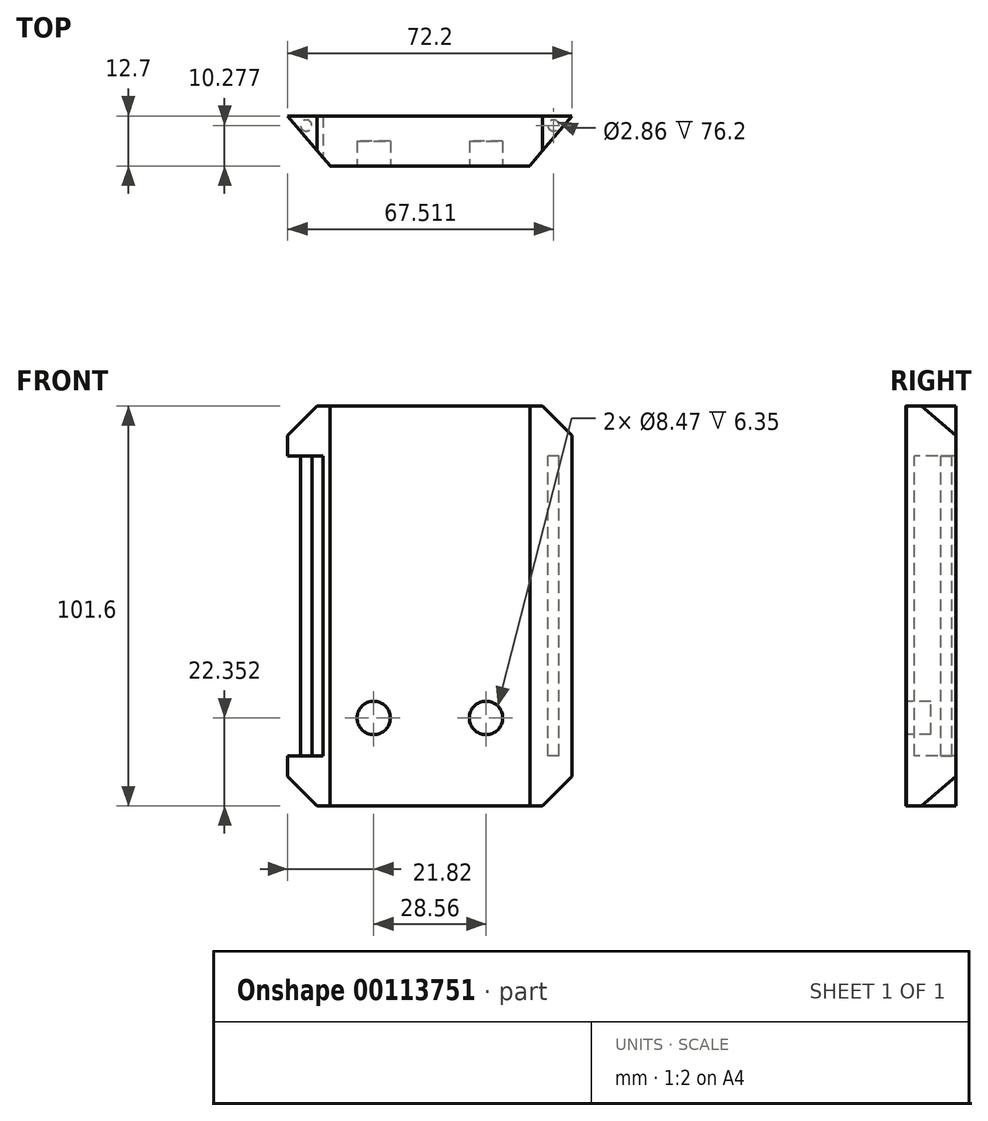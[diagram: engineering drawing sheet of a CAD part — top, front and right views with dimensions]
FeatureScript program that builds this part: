
annotation { "Feature Type Name" : "Feature", "Feature Type Description" : "" }
export const myFeature = defineFeature(function(context is Context, id is Id, definition is map)
    precondition{}
    {
        {
            var Q0;
            Q0=qCreatedBy(makeId("Front.planeOp"),FACE);
            var sketch = newSketch(context, id + "F0", { "sketchPlane" : qUnion([Q0])});
            skLineSegment(sketch, "E0.bottom", {"start": v(25.4, 50.8) * mm, "end": v(-25.4, 50.8) * mm});
            skLineSegment(sketch, "E0.top", {"start": v(25.4, -50.8) * mm, "end": v(-25.4, -50.8) * mm});
            skLineSegment(sketch, "E0.left", {"start": v(25.4, 50.8) * mm, "end": v(25.4, -50.8) * mm});
            skLineSegment(sketch, "E0.right", {"start": v(-25.4, 50.8) * mm, "end": v(-25.4, -50.8) * mm});
            skPoint(sketch, "E0.middle", {"position": v(0, 0) * mm});
            skSolve(sketch);
        }
        {
            var Q0;
            Q0=qSketchRegion(id+"F0",true);
            extrude(context, id + "F1", {"entities" : qUnion([Q0]), "depth" : 12.7 * mm});
        }
        {
            var Q0;
            Q0=qCreatedBy(makeId("Top.planeOp"),FACE);
            var sketch = newSketch(context, id + "F2", { "sketchPlane" : qUnion([Q0])});
            skLineSegment(sketch, "E1", {"start": v(25.4, 0) * mm, "end": v(36.1, 0) * mm});
            skLineSegment(sketch, "E2", {"start": v(36.1, 0) * mm, "end": v(25.4, -12.67) * mm});
            skLineSegment(sketch, "E3", {"start": v(25.4, -12.67) * mm, "end": v(25.4, 0) * mm});
            skLineSegment(sketch, "E4.MirrorCS", {"start": v(-36.1, 0) * mm, "end": v(-25.4, -12.67) * mm});
            skLineSegment(sketch, "E5.MirrorCS", {"start": v(-25.4, -12.67) * mm, "end": v(-25.4, 0) * mm});
            skLineSegment(sketch, "E6.MirrorCS", {"start": v(-25.4, 0) * mm, "end": v(-36.1, 0) * mm});
            skSolve(sketch);
        }
        {
            var Q0;
            Q0=qSketchRegion(id+"F2",true);
            extrude(context, id + "F3", {"entities" : qUnion([Q0]), "operationType" : NewBodyOperationType.ADD, "depth" : 101.6 * mm, "symmetric" : true});
        }
        {
            var Q0;
            Q0=qCreatedBy(makeId("Top.planeOp"),FACE);
            var sketch = newSketch(context, id + "F4", { "sketchPlane" : qUnion([Q0])});
            skCircle(sketch, "E7", {"center": v(-31.41, -2.42) * mm, "radius": 1.43 * mm});
            skCircle(sketch, "E8.MirrorC", {"center": v(31.41, -2.42) * mm, "radius": 1.43 * mm});
            skLineSegment(sketch, "E9.bottom", {"start": v(27.18, 1.43) * mm, "end": v(39.9, 1.43) * mm});
            skLineSegment(sketch, "E9.top", {"start": v(27.18, -11.19) * mm, "end": v(39.9, -11.19) * mm});
            skLineSegment(sketch, "E9.left", {"start": v(27.18, 1.43) * mm, "end": v(27.18, -11.19) * mm});
            skLineSegment(sketch, "E9.right", {"start": v(39.9, 1.43) * mm, "end": v(39.9, -11.19) * mm});
            skLineSegment(sketch, "E10.MirrorCS", {"start": v(-27.18, -11.19) * mm, "end": v(-39.9, -11.19) * mm});
            skLineSegment(sketch, "E11.MirrorCS", {"start": v(-39.9, 1.43) * mm, "end": v(-39.9, -11.19) * mm});
            skLineSegment(sketch, "E12.MirrorCS", {"start": v(-27.18, 1.43) * mm, "end": v(-39.9, 1.43) * mm});
            skLineSegment(sketch, "E13.MirrorCS", {"start": v(-27.18, 1.43) * mm, "end": v(-27.18, -11.19) * mm});
            skSolve(sketch);
        }
        {
            var Q0;
            Q0=makeQuery(id+"F4.imprint","IMPRINT",FACE,{"disambiguationData":[TD([[makeQuery(id+"F4.imprint","IMPRINT",EDGE,{"derivedFrom":sQuery(id+"F4.wireOp",EDGE,"E8.MirrorC")}),1.0]])]});
            var Q1;
            Q1=makeQuery(id+"F4.imprint","IMPRINT",FACE,{"disambiguationData":[TD([[makeQuery(id+"F4.imprint","IMPRINT",EDGE,{"derivedFrom":sQuery(id+"F4.wireOp",EDGE,"E7")}),-1.0]])]});
            extrude(context, id + "F5", {"entities" : qUnion([Q0, Q1]), "operationType" : NewBodyOperationType.REMOVE, "oppositeDirection" : true, "depth" : 76.2 * mm, "symmetric" : true});
        }
        {
            var Q0;
            Q0=qCreatedBy(makeId("Front.planeOp"),FACE);
            var sketch = newSketch(context, id + "F6", { "sketchPlane" : qUnion([Q0])});
            skLineSegment(sketch, "E14", {"start": v(-40.53, 38.9) * mm, "end": v(-23.28, 56.16) * mm});
            skLineSegment(sketch, "E15", {"start": v(-23.28, 56.16) * mm, "end": v(-40.53, 56.16) * mm});
            skLineSegment(sketch, "E16", {"start": v(-40.53, 56.16) * mm, "end": v(-40.53, 38.9) * mm});
            skLineSegment(sketch, "E17.MirrorCS", {"start": v(40.53, 56.16) * mm, "end": v(40.53, 38.9) * mm});
            skLineSegment(sketch, "E18.MirrorCS", {"start": v(23.28, 56.16) * mm, "end": v(40.53, 56.16) * mm});
            skLineSegment(sketch, "E19.MirrorCS", {"start": v(40.53, 38.9) * mm, "end": v(23.28, 56.16) * mm});
            skLineSegment(sketch, "E20.MirrorCS", {"start": v(-40.53, -56.16) * mm, "end": v(-40.53, -38.9) * mm});
            skLineSegment(sketch, "E21.MirrorCS", {"start": v(-23.28, -56.16) * mm, "end": v(-40.53, -56.16) * mm});
            skLineSegment(sketch, "E22.MirrorCS", {"start": v(-40.53, -38.9) * mm, "end": v(-23.28, -56.16) * mm});
            skLineSegment(sketch, "E23.MirrorCS", {"start": v(40.53, -38.9) * mm, "end": v(23.28, -56.16) * mm});
            skLineSegment(sketch, "E24.MirrorCS", {"start": v(23.28, -56.16) * mm, "end": v(40.53, -56.16) * mm});
            skLineSegment(sketch, "E25.MirrorCS", {"start": v(40.53, -56.16) * mm, "end": v(40.53, -38.9) * mm});
            skSolve(sketch);
        }
        {
            var Q0;
            Q0=makeQuery(id+"F6.imprint","IMPRINT",FACE,{"disambiguationData":[TD([[makeQuery(id+"F6.imprint","IMPRINT",EDGE,{"derivedFrom":sQuery(id+"F6.wireOp",EDGE,"E17.MirrorCS")}),-1.0]])]});
            var Q1;
            Q1=makeQuery(id+"F6.imprint","IMPRINT",FACE,{"disambiguationData":[TD([[makeQuery(id+"F6.imprint","IMPRINT",EDGE,{"derivedFrom":sQuery(id+"F6.wireOp",EDGE,"E20.MirrorCS")}),-1.0]])]});
            var Q2;
            Q2=makeQuery(id+"F6.imprint","IMPRINT",FACE,{"disambiguationData":[TD([[makeQuery(id+"F6.imprint","IMPRINT",EDGE,{"derivedFrom":sQuery(id+"F6.wireOp",EDGE,"E23.MirrorCS")}),1.0]])]});
            var Q3;
            Q3=makeQuery(id+"F6.imprint","IMPRINT",FACE,{"disambiguationData":[TD([[makeQuery(id+"F6.imprint","IMPRINT",EDGE,{"derivedFrom":sQuery(id+"F6.wireOp",EDGE,"E14")}),1.0]])]});
            extrude(context, id + "F7", {"entities" : qUnion([Q0, Q1, Q2, Q3]), "operationType" : NewBodyOperationType.REMOVE, "endBound" : BoundingType.THROUGH_ALL, "depth" : 25.4 * mm});
        }
        {
            var Q0;
            Q0=makeQuery(id+"F1.opExtrude","CAP_FACE",FACE,{"disambiguationData":[OSD([sQuery(id+"F0.wireOp",EDGE,"E0.bottom"),sQuery(id+"F0.wireOp",EDGE,"E0.top"),sQuery(id+"F0.wireOp",EDGE,"E0.left"),sQuery(id+"F0.wireOp",EDGE,"E0.right")])],"isStart":false});
            var sketch = newSketch(context, id + "F8", { "sketchPlane" : qUnion([Q0])});
            skLineSegment(sketch, "E26.bottom", {"start": v(22.23, 28.57) * mm, "end": v(-22.22, 28.57) * mm});
            skLineSegment(sketch, "E26.top", {"start": v(22.22, -28.58) * mm, "end": v(-22.22, -28.58) * mm});
            skLineSegment(sketch, "E26.left", {"start": v(22.22, 28.57) * mm, "end": v(22.22, -28.58) * mm});
            skLineSegment(sketch, "E26.right", {"start": v(-22.23, 28.57) * mm, "end": v(-22.23, -28.58) * mm});
            skPoint(sketch, "E26.middle", {"position": v(0, 0) * mm});
            skArc(sketch, "E27", {"start": v(22.23, 28.58) * mm, "mid": v(0, 50.8) * mm, "end": v(-22.23, 28.57) * mm});
            skArc(sketch, "E28", {"start": v(-22.23, -28.58) * mm, "mid": v(0, -50.8) * mm, "end": v(22.23, -28.58) * mm});
            skSolve(sketch);
        }
        {
            var Q0;
            {var subQ1=sQuery(id+"F8.wireOp",EDGE,"E26.right");Q0=makeQuery(id+"F8.imprint","IMPRINT",FACE,{"disambiguationData":[TD([[makeQuery(id+"F8.imprint","IMPRINT",EDGE,{"derivedFrom":subQ1}),-1.0]])]});}
            var sketch = newSketch(context, id + "F9", { "sketchPlane" : qUnion([Q0])});
            skCircle(sketch, "E29", {"center": v(-14.28, -28.45) * mm, "radius": 4.23 * mm});
            skCircle(sketch, "E30.MirrorC", {"center": v(14.28, -28.45) * mm, "radius": 4.23 * mm});
            skSolve(sketch);
        }
        {
            var Q0;
            Q0 = qSketchRegion(id + "F9", true);
            extrude(context, id + "F10", {"entities" : qUnion([Q0]), "operationType" : NewBodyOperationType.REMOVE, "oppositeDirection" : true, "depth" : 6.35 * mm});
        }
    });
